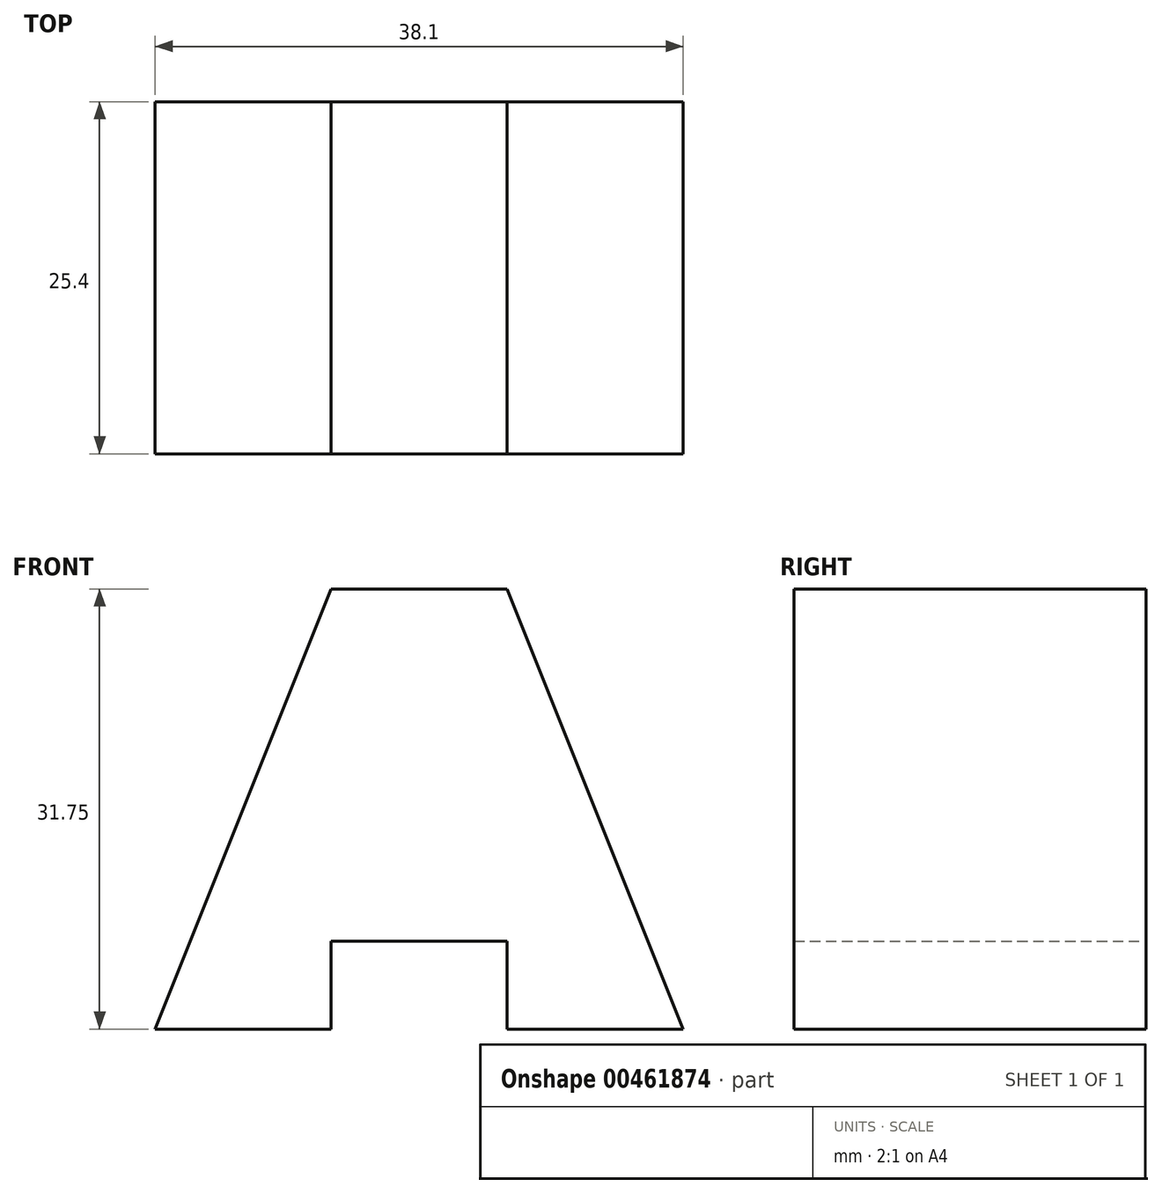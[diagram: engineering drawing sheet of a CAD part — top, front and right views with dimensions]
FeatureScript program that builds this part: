
annotation { "Feature Type Name" : "Feature", "Feature Type Description" : "" }
export const myFeature = defineFeature(function(context is Context, id is Id, definition is map)
    precondition{}
    {
        {
            var Q0;
            Q0=qCreatedBy(makeId("Front.planeOp"),FACE);
            var sketch = newSketch(context, id + "F0", { "sketchPlane" : qUnion([Q0])});
            skLineSegment(sketch, "E0", {"start": v(0, 0) * mm, "end": v(12.7, 0) * mm});
            skLineSegment(sketch, "E1", {"start": v(12.7, 0) * mm, "end": v(12.7, 6.35) * mm});
            skLineSegment(sketch, "E2", {"start": v(12.7, 6.35) * mm, "end": v(25.4, 6.35) * mm});
            skLineSegment(sketch, "E3", {"start": v(25.4, 6.35) * mm, "end": v(25.4, 0) * mm});
            skLineSegment(sketch, "E4", {"start": v(25.4, 0) * mm, "end": v(38.1, 0) * mm});
            skLineSegment(sketch, "E5", {"start": v(38.1, 0) * mm, "end": v(25.4, 31.75) * mm});
            skLineSegment(sketch, "E6", {"start": v(25.4, 31.75) * mm, "end": v(12.7, 31.75) * mm});
            skLineSegment(sketch, "E7", {"start": v(12.7, 31.75) * mm, "end": v(0, 0) * mm});
            skSolve(sketch);
        }
        {
            var Q0;
            Q0=makeQuery(id+"F0.imprint","IMPRINT",FACE,{"disambiguationData":[TD([[makeQuery(id+"F0.imprint","IMPRINT",EDGE,{"derivedFrom":sQuery(id+"F0.wireOp",EDGE,"E0")}),1.0]])]});
            extrude(context, id + "F1", {"entities" : qUnion([Q0]), "depth" : 25.4 * mm});
        }
    });
